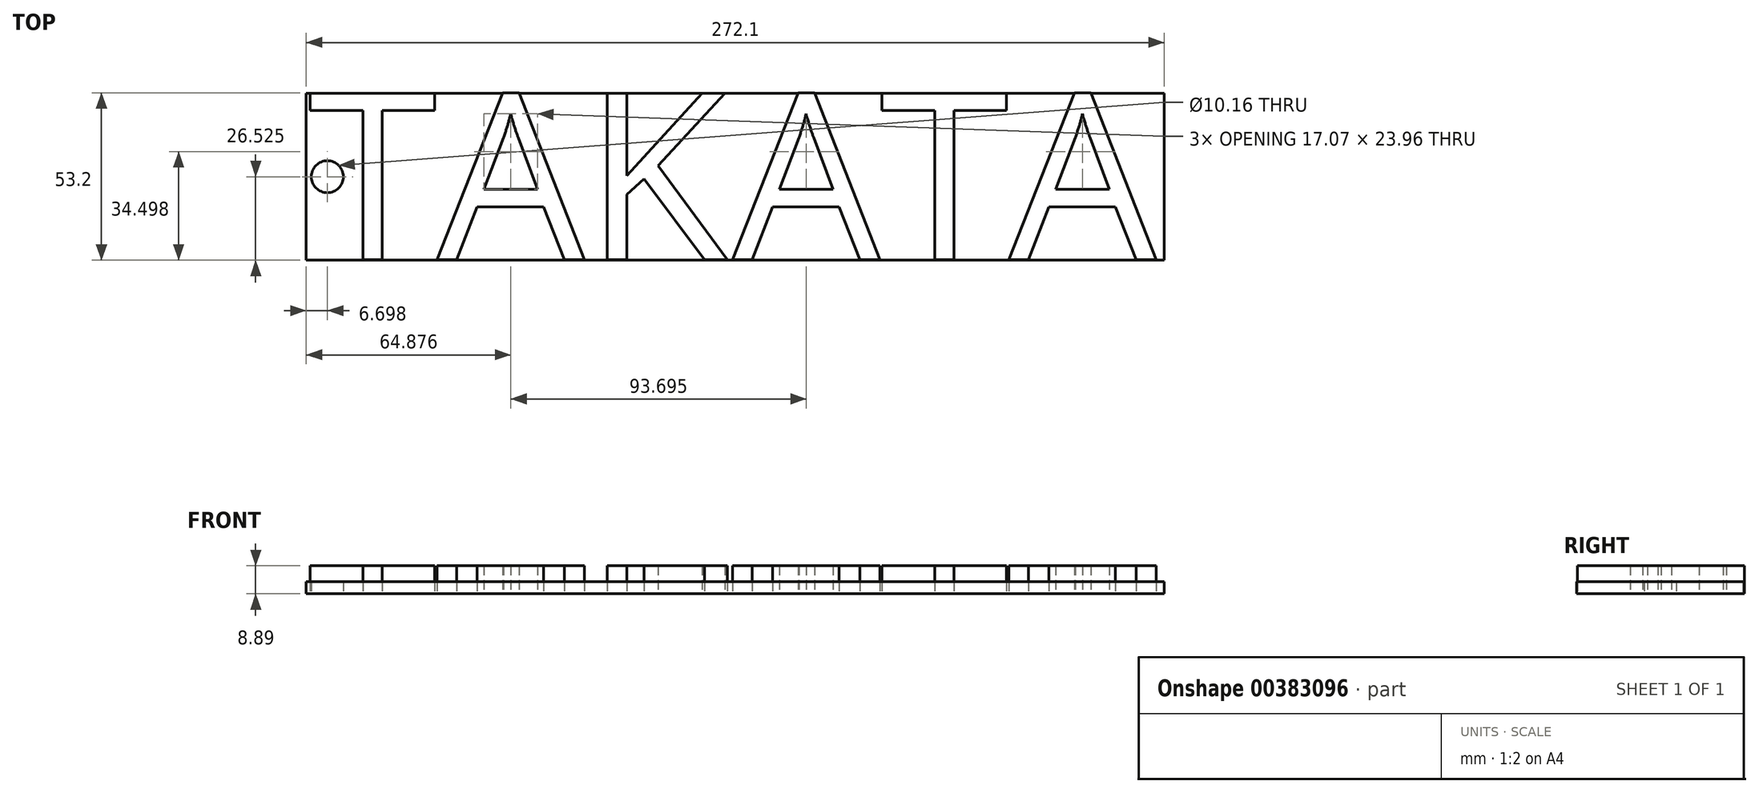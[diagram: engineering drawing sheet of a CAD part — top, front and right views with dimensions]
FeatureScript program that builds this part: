
annotation { "Feature Type Name" : "Feature", "Feature Type Description" : "" }
export const myFeature = defineFeature(function(context is Context, id is Id, definition is map)
    precondition{}
    {
        {
            var Q0;
            Q0=qCreatedBy(makeId("Top.planeOp"),FACE);
            var sketch = newSketch(context, id + "F0", { "sketchPlane" : qUnion([Q0])});
            skText(sketch, "E0", { "text": "TAKATA", "fontName": "OpenSans-Regular.ttf"});
            const initialGuessF0  = {"E0": [-0.05454, -0.0166, 1, 0, 0.05321]};
            skSetInitialGuess(sketch, initialGuessF0);
            skSolve(sketch);
        }
        {
            var Q0;
            Q0=qCreatedBy(makeId("Top.planeOp"),FACE);
            var sketch = newSketch(context, id + "F1", { "sketchPlane" : qUnion([Q0])});
            skLineSegment(sketch, "E1.bottom", {"start": v(-55.12, 36.23) * mm, "end": v(216.98, 36.23) * mm});
            skLineSegment(sketch, "E1.top", {"start": v(-55.12, -16.82) * mm, "end": v(216.98, -16.82) * mm});
            skLineSegment(sketch, "E1.left", {"start": v(-55.12, 36.23) * mm, "end": v(-55.12, -16.82) * mm});
            skLineSegment(sketch, "E1.right", {"start": v(216.98, 36.23) * mm, "end": v(216.98, -16.82) * mm});
            skCircle(sketch, "E2", {"center": v(-48.42, 9.7) * mm, "radius": 6.7 * mm});
            skPoint(sketch, "E2.centerSnap0", {"position": v(-55.12, 9.7) * mm});
            skSolve(sketch);
        }
        {
            var Q0;
            Q0 = qSketchRegion(id + "F0", true);
            extrude(context, id + "F2", {"entities" : qUnion([Q0]), "depth" : 8.9 * mm});
        }
        {
            var Q0;
            Q0 = qSketchRegion(id + "F1", true);
            extrude(context, id + "F3", {"entities" : qUnion([Q0]), "depth" : 3.8 * mm});
        }
        {
            var Q0;
            Q0=sQuery(id+"F1.wireOp",VERTEX,"E2.center");
            var Q1;
            Q1=makeQuery(id+"F3.opExtrude","SWEPT_BODY",BODY,{"disambiguationData":[OSD([sQuery(id+"F1.wireOp",EDGE,"E1.bottom"),sQuery(id+"F1.wireOp",EDGE,"E1.top"),sQuery(id+"F1.wireOp",EDGE,"E1.left"),sQuery(id+"F1.wireOp",EDGE,"E1.right")])]});
            hole(context, id + "F4", {"style" : HoleStyle.SIMPLE, "endStyle" : HoleEndStyle.THROUGH, "oppositeDirection" : true, "holeDiameter" : 10.16 * mm, "isTappedThrough" : true, "tappedDepth" : 12.7 * mm, "tapClearance" : 3, "locations" : qUnion([Q0]), "scope" : qUnion([Q1])});
        }
    });
